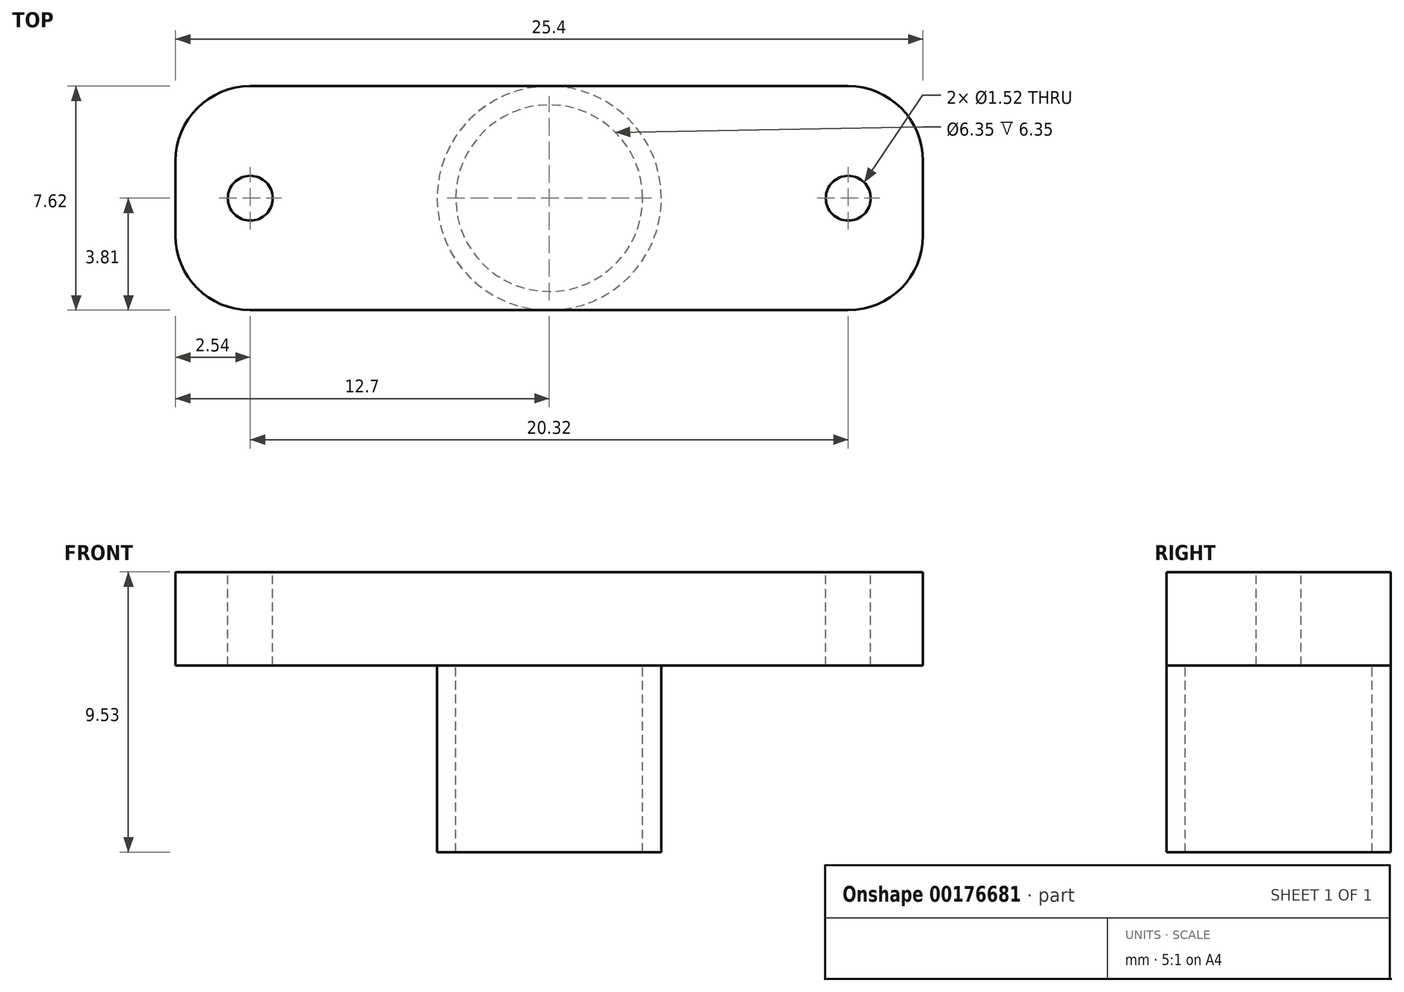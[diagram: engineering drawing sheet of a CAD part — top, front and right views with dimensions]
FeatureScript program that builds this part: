
annotation { "Feature Type Name" : "Feature", "Feature Type Description" : "" }
export const myFeature = defineFeature(function(context is Context, id is Id, definition is map)
    precondition{}
    {
        {
            var Q0;
            Q0=qCreatedBy(makeId("Top.planeOp"),FACE);
            var sketch = newSketch(context, id + "F0", { "sketchPlane" : qUnion([Q0])});
            skLineSegment(sketch, "E0.bottom", {"start": v(12.7, 3.81) * mm, "end": v(-12.7, 3.81) * mm});
            skLineSegment(sketch, "E0.top", {"start": v(12.7, -3.81) * mm, "end": v(-12.7, -3.81) * mm});
            skLineSegment(sketch, "E0.left", {"start": v(12.7, 3.81) * mm, "end": v(12.7, -3.81) * mm});
            skLineSegment(sketch, "E0.right", {"start": v(-12.7, 3.81) * mm, "end": v(-12.7, -3.81) * mm});
            skPoint(sketch, "E0.middle", {"position": v(0, 0) * mm});
            skSolve(sketch);
        }
        {
            var Q0;
            Q0 = qSketchRegion(id + "F0", true);
            extrude(context, id + "F1", {"entities" : qUnion([Q0]), "depth" : 3.17 * mm});
        }
        {
            var Q0;
            Q0=makeQuery(id+"F1.opExtrude","SWEPT_EDGE",EDGE,{"disambiguationData":[OSD([sQuery(id+"F0.wireOp",EDGE,"E0.top"),sQuery(id+"F0.wireOp",EDGE,"E0.right")])]});
            var Q1;
            Q1=makeQuery(id+"F1.opExtrude","SWEPT_EDGE",EDGE,{"disambiguationData":[OSD([sQuery(id+"F0.wireOp",EDGE,"E0.top"),sQuery(id+"F0.wireOp",EDGE,"E0.left")])]});
            var Q2;
            Q2=makeQuery(id+"F1.opExtrude","SWEPT_EDGE",EDGE,{"disambiguationData":[OSD([sQuery(id+"F0.wireOp",EDGE,"E0.bottom"),sQuery(id+"F0.wireOp",EDGE,"E0.left")])]});
            var Q3;
            Q3=makeQuery(id+"F1.opExtrude","SWEPT_EDGE",EDGE,{"disambiguationData":[OSD([sQuery(id+"F0.wireOp",EDGE,"E0.bottom"),sQuery(id+"F0.wireOp",EDGE,"E0.right")])]});
            fillet(context, id + "F2", {"entities" : qUnion([Q0, Q1, Q2, Q3]), "radius" : 2.54 * mm, "tangentPropagation" : true, "allowEdgeOverflow" : false});
        }
        {
            var Q0;
            Q0=makeQuery(id+"F1.opExtrude","CAP_FACE",FACE,{"disambiguationData":[OSD([sQuery(id+"F0.wireOp",EDGE,"E0.bottom"),sQuery(id+"F0.wireOp",EDGE,"E0.top"),sQuery(id+"F0.wireOp",EDGE,"E0.left"),sQuery(id+"F0.wireOp",EDGE,"E0.right")])],"isStart":true});
            var sketch = newSketch(context, id + "F3", { "sketchPlane" : qUnion([Q0])});
            skCircle(sketch, "E1", {"center": v(0, 0) * mm, "radius": 3.81 * mm});
            skCircle(sketch, "E2", {"center": v(0, 0) * mm, "radius": 3.18 * mm});
            skSolve(sketch);
        }
        {
            var Q0;
            Q0 = qSketchRegion(id + "F3", true);
            extrude(context, id + "F4", {"entities" : qUnion([Q0]), "operationType" : NewBodyOperationType.ADD, "depth" : 6.35 * mm});
        }
        {
            var Q0;
            Q0=makeQuery(id+"F1.opExtrude","CAP_FACE",FACE,{"disambiguationData":[OSD([sQuery(id+"F0.wireOp",EDGE,"E0.bottom"),sQuery(id+"F0.wireOp",EDGE,"E0.top"),sQuery(id+"F0.wireOp",EDGE,"E0.left"),sQuery(id+"F0.wireOp",EDGE,"E0.right")])],"isStart":false});
            var sketch = newSketch(context, id + "F5", { "sketchPlane" : qUnion([Q0])});
            skCircle(sketch, "E3", {"center": v(-10.16, 0) * mm, "radius": 0.76 * mm});
            skCircle(sketch, "E4", {"center": v(10.16, 0) * mm, "radius": 0.76 * mm});
            skSolve(sketch);
        }
        {
            var Q0;
            Q0 = qSketchRegion(id + "F5", true);
            extrude(context, id + "F6", {"entities" : qUnion([Q0]), "operationType" : NewBodyOperationType.REMOVE, "endBound" : BoundingType.THROUGH_ALL, "oppositeDirection" : true, "depth" : 25.4 * mm});
        }
    });
